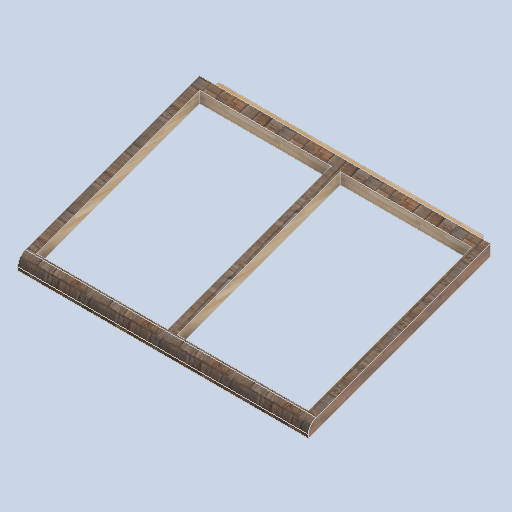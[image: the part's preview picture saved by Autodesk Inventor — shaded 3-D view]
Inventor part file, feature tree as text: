
AUTODESK INVENTOR PART (.ipt)
format: ipt  version: 2024.2 (Build 282272000, 272)  size: 419,840 bytes
history: native  units: mm
features: sketch x6, extrude x4, plane x2, projected_geometry x2, fillet x1
ambient origin geometry x8: Origin, YZ Plane, XZ Plane, XY Plane, X Axis, Y Axis, Z Axis, Center Point
bodies: Solid1 (feature_tree)
feature tree (15):
  extrude  "Extrusion1"  Depth=50.0mm TaperAngle=0.0deg
  plane  "Work Plane1"
  plane  "Work Plane2"
  extrude  "Extrusion2"  Depth=2500.0mm
  extrude  "Extrusion3"  Depth=150.0mm
  sketch  "Sketch4"  dims[d8=3752.0mm d9=0.0mm d10=0.0mm d11=0.0mm]
  sketch  "Sketch5"  dims[d12=400.0mm]
  fillet  "Fillet1"  Radius=3752.111457mm
  extrude  "Extrusion5"  TaperAngle=0.0deg  [1 undecoded]
  sketch  "Sketch6"  dims[d13=10.0mm d14=20.0mm d15=400.0mm d16=20.0mm d17=400.0mm d18=20.0mm d19=400.0mm d20=20.0mm d21=400.0mm d22=20.0mm d23=120.0mm d24=120.0mm d25=120.0mm d26=120.0mm d29=150.0mm d32=0.0mm d33=0.0mm]
  sketch  "Sketch1"  dims[d0=150.0mm d1=50.0mm d2=0.0mm]
  sketch  "Sketch2"  dims[d3=0.0mm d4=2500.0mm]
  sketch  "Sketch3"  dims[d5=12.217305mm d6=150.0mm d7=3752.111457mm]
  projected_geometry  "Projected Loop1"
  projected_geometry  "Projected Loop2"
note: 1 required parameter value undecoded (feature->parameter linkage not recoverable at this tier; creation-order binding heuristic only, values carry confidence <= 0.55)
